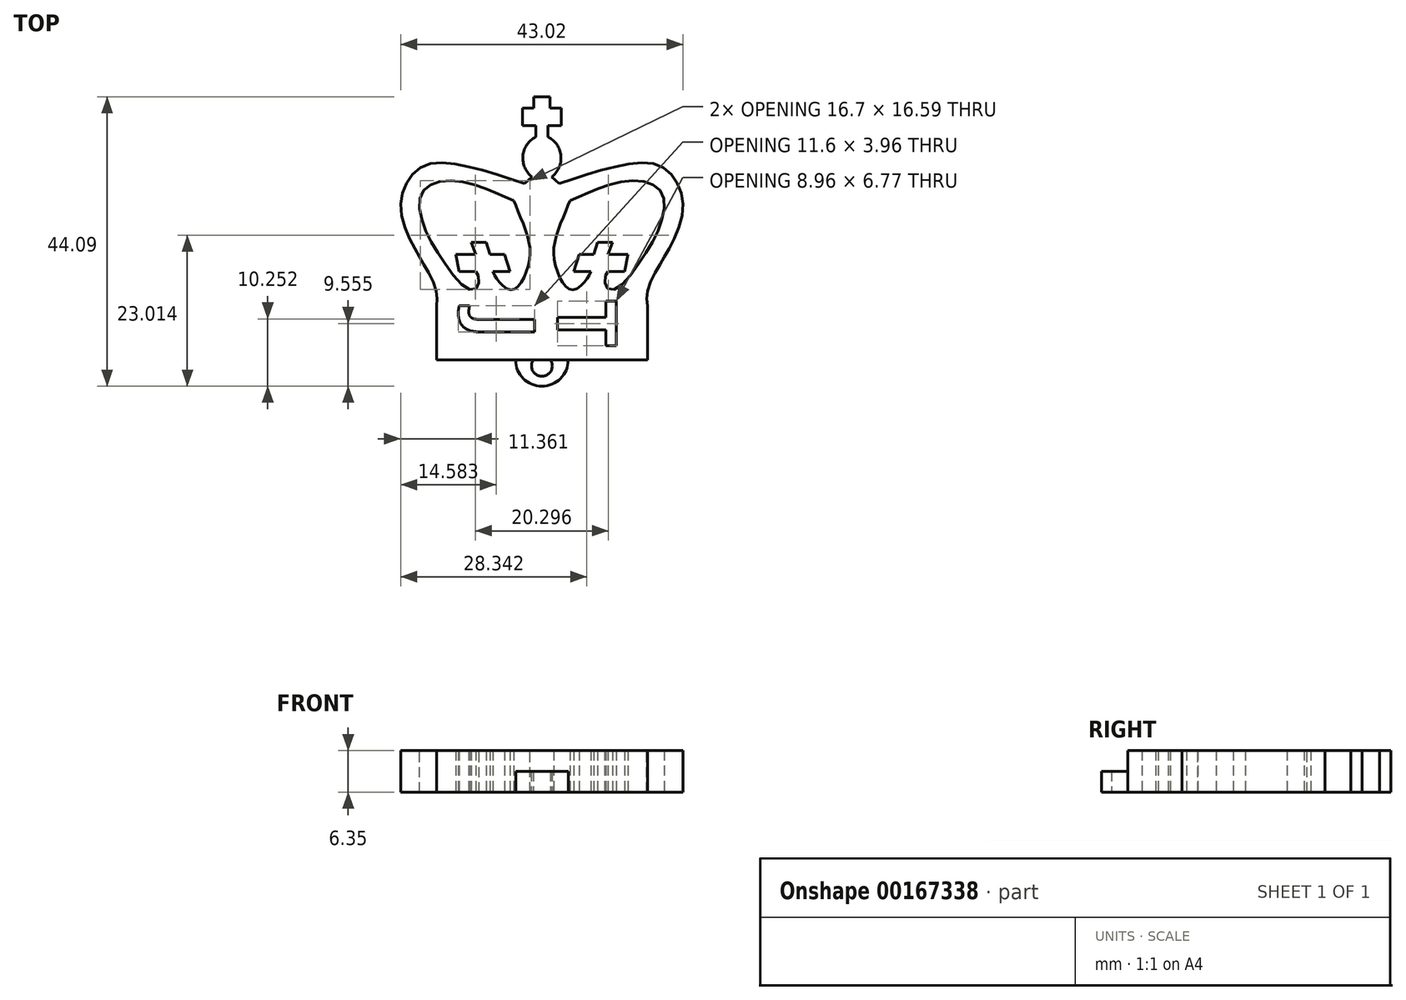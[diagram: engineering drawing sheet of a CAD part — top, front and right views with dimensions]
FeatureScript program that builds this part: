
annotation { "Feature Type Name" : "Feature", "Feature Type Description" : "" }
export const myFeature = defineFeature(function(context is Context, id is Id, definition is map)
    precondition{}
    {
        {
            var Q0;
            Q0=qCreatedBy(makeId("Top.planeOp"),FACE);
            var sketch = newSketch(context, id + "F0", { "sketchPlane" : qUnion([Q0])});
            skFitSpline(sketch, "E0", {"points": [v(-4.35, 3.8) * mm, v(-12.5, 6.26) * mm, v(-19.04, 6.69) * mm, v(-22.26, 3.9) * mm, v(-23.12, -0.82) * mm, v(-21.08, -6.08) * mm, v(-19.36, -9.08) * mm, v(-17.76, -12.62) * mm, v(-17.76, -14.88) * mm], "startDerivative": vector(-48.77, 16.18) * mm, "endDerivative": vector(-3.27, -24.62) * mm});
            skLineSegment(sketch, "E1", {"start": v(-4.35, 3.8) * mm, "end": v(-3.17, 4.76) * mm});
            skLineSegment(sketch, "E2", {"start": v(-2.63, 10.87) * mm, "end": v(-2.63, 12.59) * mm});
            skLineSegment(sketch, "E3", {"start": v(-2.63, 12.59) * mm, "end": v(-4.67, 12.59) * mm});
            skLineSegment(sketch, "E4", {"start": v(-4.67, 12.59) * mm, "end": v(-4.67, 15.27) * mm});
            skLineSegment(sketch, "E5", {"start": v(-4.67, 15.27) * mm, "end": v(-2.95, 15.27) * mm});
            skLineSegment(sketch, "E6", {"start": v(-2.95, 15.27) * mm, "end": v(-2.95, 16.99) * mm});
            skLineSegment(sketch, "E7", {"start": v(-2.95, 16.99) * mm, "end": v(-1.7, 16.99) * mm});
            skArc(sketch, "E8", {"start": v(-2.63, 10.87) * mm, "mid": v(-4.59, 7.96) * mm, "end": v(-3.17, 4.76) * mm});
            skFitSpline(sketch, "E9", {"points": [v(-5.96, 1.14) * mm, v(-9.39, 2.61) * mm, v(-14.1, 4.11) * mm, v(-18.4, 3.68) * mm, v(-20.22, 1.65) * mm, v(-19.69, -2.65) * mm, v(-17, -7.58) * mm, v(-13.25, -12.09) * mm, v(-11.64, -12.2) * mm, v(-11.32, -10.48) * mm, v(-11.75, -9.62) * mm], "startDerivative": vector(-31.67, 15.2) * mm, "endDerivative": vector(-9.86, 13.12) * mm});
            skFitSpline(sketch, "E10", {"points": [v(-9.17, -9.62) * mm, v(-8.1, -11.34) * mm, v(-6.28, -12.4) * mm, v(-4.56, -10.8) * mm, v(-3.49, -6.83) * mm, v(-4.35, -2.86) * mm, v(-5.96, 1.14) * mm], "startDerivative": vector(6.47, -12.8) * mm, "endDerivative": vector(-5.62, 13.35) * mm});
            skLineSegment(sketch, "E11", {"start": v(-11.75, -9.62) * mm, "end": v(-14.3, -9.62) * mm});
            skLineSegment(sketch, "E12", {"start": v(-14.3, -9.62) * mm, "end": v(-14.8, -7.06) * mm});
            skLineSegment(sketch, "E13", {"start": v(-14.8, -7.06) * mm, "end": v(-11.75, -7.06) * mm});
            skLineSegment(sketch, "E14", {"start": v(-11.75, -7.06) * mm, "end": v(-12.44, -5.17) * mm});
            skLineSegment(sketch, "E15", {"start": v(-12.44, -5.17) * mm, "end": v(-10.18, -5.17) * mm});
            skLineSegment(sketch, "E16", {"start": v(-10.18, -5.17) * mm, "end": v(-9.6, -7.06) * mm});
            skLineSegment(sketch, "E17", {"start": v(-9.6, -7.06) * mm, "end": v(-7.38, -7.06) * mm});
            skLineSegment(sketch, "E18", {"start": v(-7.38, -7.06) * mm, "end": v(-6.53, -9.62) * mm});
            skLineSegment(sketch, "E19", {"start": v(-6.53, -9.62) * mm, "end": v(-9.17, -9.62) * mm});
            skLineSegment(sketch, "E20.MirrorCS", {"start": v(-0.43, 15.27) * mm, "end": v(-0.43, 16.99) * mm});
            skLineSegment(sketch, "E21.MirrorCS", {"start": v(1.29, 15.27) * mm, "end": v(-0.43, 15.27) * mm});
            skLineSegment(sketch, "E22.MirrorCS", {"start": v(-0.75, 10.87) * mm, "end": v(-0.75, 12.59) * mm});
            skLineSegment(sketch, "E23.MirrorCS", {"start": v(0.96, 3.8) * mm, "end": v(-0.22, 4.76) * mm});
            skLineSegment(sketch, "E24.MirrorCS", {"start": v(8.37, -7.06) * mm, "end": v(9.06, -5.17) * mm});
            skLineSegment(sketch, "E25.MirrorCS", {"start": v(6.8, -5.17) * mm, "end": v(6.22, -7.06) * mm});
            skLineSegment(sketch, "E26.MirrorCS", {"start": v(3.15, -9.62) * mm, "end": v(5.8, -9.62) * mm});
            skLineSegment(sketch, "E27.MirrorCS", {"start": v(9.06, -5.17) * mm, "end": v(6.8, -5.17) * mm});
            skLineSegment(sketch, "E28.MirrorCS", {"start": v(6.22, -7.06) * mm, "end": v(4, -7.06) * mm});
            skLineSegment(sketch, "E29.MirrorCS", {"start": v(8.37, -9.62) * mm, "end": v(10.92, -9.62) * mm});
            skFitSpline(sketch, "E30.MirrorCS", {"points": [v(5.8, -9.62) * mm, v(4.72, -11.34) * mm, v(2.9, -12.4) * mm, v(1.18, -10.8) * mm, v(0.1, -6.83) * mm, v(0.96, -2.86) * mm, v(2.58, 1.14) * mm], "startDerivative": vector(-6.47, -12.8) * mm, "endDerivative": vector(5.62, 13.35) * mm});
            skFitSpline(sketch, "E31.MirrorCS", {"points": [v(2.58, 1.14) * mm, v(6, 2.61) * mm, v(10.73, 4.11) * mm, v(15.02, 3.68) * mm, v(16.84, 1.65) * mm, v(16.3, -2.65) * mm, v(13.62, -7.58) * mm, v(9.87, -12.09) * mm, v(8.26, -12.2) * mm, v(7.94, -10.48) * mm, v(8.37, -9.62) * mm], "startDerivative": vector(31.67, 15.2) * mm, "endDerivative": vector(9.86, 13.12) * mm});
            skArc(sketch, "E32.MirrorCS", {"start": v(-0.75, 10.87) * mm, "mid": v(1.2, 7.96) * mm, "end": v(-0.22, 4.76) * mm});
            skLineSegment(sketch, "E33.MirrorCS", {"start": v(1.29, 12.59) * mm, "end": v(1.29, 15.27) * mm});
            skLineSegment(sketch, "E34.MirrorCS", {"start": v(-0.75, 12.59) * mm, "end": v(1.29, 12.59) * mm});
            skFitSpline(sketch, "E35.MirrorCS", {"points": [v(0.96, 3.8) * mm, v(9.12, 6.26) * mm, v(15.66, 6.69) * mm, v(18.88, 3.9) * mm, v(19.74, -0.82) * mm, v(17.7, -6.08) * mm, v(15.98, -9.08) * mm, v(14.37, -12.62) * mm, v(14.37, -14.88) * mm], "startDerivative": vector(48.77, 16.18) * mm, "endDerivative": vector(3.27, -24.62) * mm});
            skLineSegment(sketch, "E36.MirrorCS", {"start": v(11.43, -7.06) * mm, "end": v(8.37, -7.06) * mm});
            skLineSegment(sketch, "E37.MirrorCS", {"start": v(10.92, -9.62) * mm, "end": v(11.43, -7.06) * mm});
            skLineSegment(sketch, "E38.MirrorCS", {"start": v(4, -7.06) * mm, "end": v(3.15, -9.62) * mm});
            skLineSegment(sketch, "E39.MirrorCS", {"start": v(-0.43, 16.99) * mm, "end": v(-1.7, 16.99) * mm});
            skLineSegment(sketch, "E40", {"start": v(14.37, -14.88) * mm, "end": v(14.37, -23.1) * mm});
            skLineSegment(sketch, "E41", {"start": v(14.37, -23.1) * mm, "end": v(-17.76, -23.1) * mm});
            skLineSegment(sketch, "E42", {"start": v(-17.76, -14.88) * mm, "end": v(-17.76, -23.1) * mm});
            skText(sketch, "E43", { "text": "T", "fontName": "OpenSans-Bold.ttf"});
            skText(sketch, "E44", { "text": "J", "fontName": "OpenSans-Bold.ttf"});
            skArc(sketch, "E45", {"start": v(-5.7, -23.1) * mm, "mid": v(-1.7, -27.1) * mm, "end": v(2.3, -23.1) * mm});
            skArc(sketch, "E46", {"start": v(-3, -23.1) * mm, "mid": v(-1.7, -25.58) * mm, "end": v(-0.38, -23.1) * mm});
            const initialGuessF0  = {"E43": [0.00066, -0.01391, 0, -1, 0.00904], "E44": [-0.01178, -0.0158, 0, -1, 0.00904]};
            skSetInitialGuess(sketch, initialGuessF0);
            skSolve(sketch);
        }
        {
            var Q0;
            Q0=makeQuery(id+"F0.imprint","IMPRINT",FACE,{"disambiguationData":[TD([[makeQuery(id+"F0.imprint","IMPRINT",EDGE,{"derivedFrom":sQuery(id+"F0.wireOp",EDGE,"E0")}),1.0]])]});
            extrude(context, id + "F1", {"entities" : qUnion([Q0]), "depth" : 6.35 * mm, "offsetDistance" : 25 * mm});
        }
        {
            var Q0;
            {var subQ0=sQuery(id+"F0.wireOp",EDGE,"E45");Q0=makeQuery(id+"F0.imprint","IMPRINT",FACE,{"disambiguationData":[TD([[makeQuery(id+"F0.imprint","IMPRINT",EDGE,{"derivedFrom":subQ0}),1.0]])]});}
            extrude(context, id + "F2", {"entities" : qUnion([Q0]), "operationType" : NewBodyOperationType.ADD, "depth" : 3.17 * mm, "offsetDistance" : 25 * mm});
        }
    });
